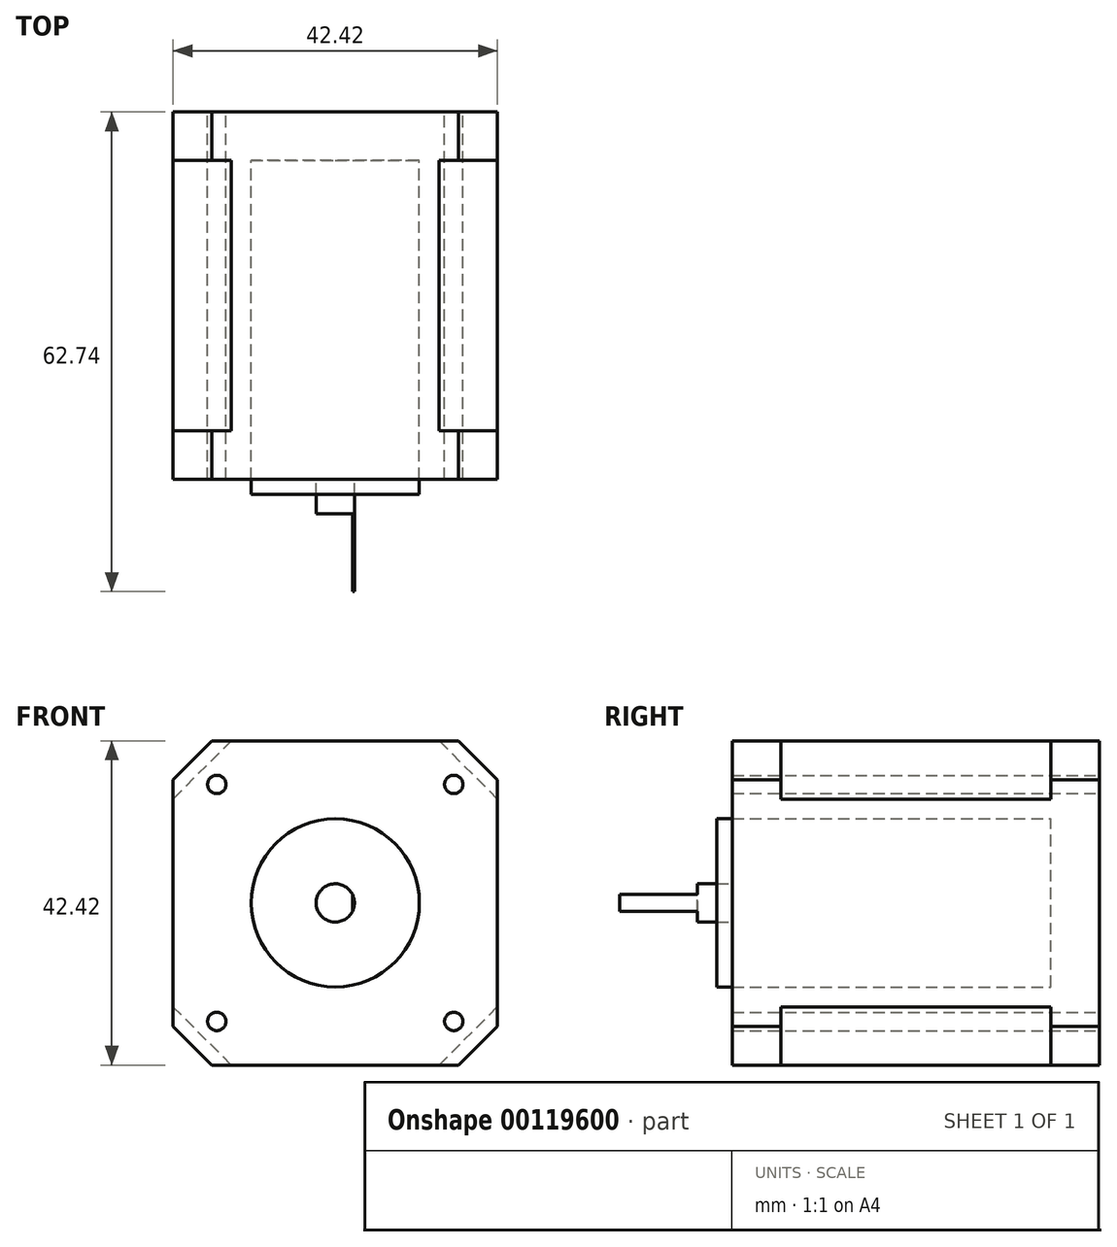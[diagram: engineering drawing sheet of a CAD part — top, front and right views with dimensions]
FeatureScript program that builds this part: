
annotation { "Feature Type Name" : "Feature", "Feature Type Description" : "" }
export const myFeature = defineFeature(function(context is Context, id is Id, definition is map)
    precondition{}
    {
        {
            var Q0;
            Q0=qCreatedBy(makeId("Front.planeOp"),FACE);
            var sketch = newSketch(context, id + "F0", { "sketchPlane" : qUnion([Q0])});
            skPoint(sketch, "E0.middle", {"position": v(0, 0) * mm});
            skLineSegment(sketch, "E1.bottom", {"start": v(-16.13, -21.2) * mm, "end": v(16.13, -21.2) * mm});
            skLineSegment(sketch, "E1.top", {"start": v(-16.13, 21.21) * mm, "end": v(16.13, 21.21) * mm});
            skLineSegment(sketch, "E1.left", {"start": v(-21.21, -16.13) * mm, "end": v(-21.21, 16.13) * mm});
            skLineSegment(sketch, "E1.right", {"start": v(21.2, -16.13) * mm, "end": v(21.2, 16.13) * mm});
            skCircle(sketch, "E2", {"center": v(0, 0) * mm, "radius": 11 * mm});
            skCircle(sketch, "E3", {"center": v(0, 0) * mm, "radius": 2.5 * mm});
            skCircle(sketch, "E4", {"center": v(15.5, 15.5) * mm, "radius": 1.2 * mm});
            skCircle(sketch, "E5.MirrorC", {"center": v(-15.5, 15.5) * mm, "radius": 1.2 * mm});
            skCircle(sketch, "E6.MirrorC", {"center": v(15.5, -15.5) * mm, "radius": 1.2 * mm});
            skCircle(sketch, "E7.MirrorC", {"center": v(-15.5, -15.5) * mm, "radius": 1.2 * mm});
            skLineSegment(sketch, "E8", {"start": v(-16.13, 21.21) * mm, "end": v(-21.21, 16.13) * mm});
            skLineSegment(sketch, "E9", {"start": v(-21.21, -16.13) * mm, "end": v(-16.13, -21.2) * mm});
            skLineSegment(sketch, "E10", {"start": v(16.13, -21.2) * mm, "end": v(21.2, -16.13) * mm});
            skLineSegment(sketch, "E11", {"start": v(21.2, 16.13) * mm, "end": v(16.13, 21.21) * mm});
            skLineSegment(sketch, "E12", {"start": v(-13.6, 21.21) * mm, "end": v(-21.21, 13.59) * mm});
            skLineSegment(sketch, "E13", {"start": v(-21.21, -13.59) * mm, "end": v(-13.59, -21.2) * mm});
            skLineSegment(sketch, "E14", {"start": v(13.59, -21.2) * mm, "end": v(21.2, -13.59) * mm});
            skLineSegment(sketch, "E15", {"start": v(21.2, 13.6) * mm, "end": v(13.59, 21.21) * mm});
            skLineSegment(sketch, "E16.bottom", {"start": v(2.75, -2.5) * mm, "end": v(2.25, -2.5) * mm});
            skLineSegment(sketch, "E16.top", {"start": v(2.75, 2.5) * mm, "end": v(2.25, 2.5) * mm});
            skLineSegment(sketch, "E16.left", {"start": v(2.75, -2.5) * mm, "end": v(2.75, 2.5) * mm});
            skLineSegment(sketch, "E16.right", {"start": v(2.25, -2.5) * mm, "end": v(2.25, 2.5) * mm});
            skPoint(sketch, "E16.middle", {"position": v(2.5, 0) * mm});
            skSolve(sketch);
        }
        {
            var Q0;
            {var subQ0=sQuery(id+"F0.wireOp",EDGE,"E16.right");var subQ1=sQuery(id+"F0.wireOp",EDGE,"E3");var subQ2=makeQuery(id+"F0.imprint","INTERSECT",VERTEX,{"disambiguationData":[OD(0.0)],"derivedFrom":[subQ1,subQ0]});Q0=makeQuery(id+"F0.imprint","IMPRINT",FACE,{"disambiguationData":[TD([[makeQuery(id+"F0.imprint","IMPRINT",EDGE,{"disambiguationData":[TD([[subQ2,1.0]])],"derivedFrom":subQ1}),1.0]])]});}
            extrude(context, id + "F1", {"entities" : qUnion([Q0]), "depth" : 62.74 * mm, "hasSecondDirection" : true, "secondDirectionOppositeDirection" : false, "secondDirectionDepth" : 52.58 * mm});
        }
        {
            var Q0;
            {var subQ0=sQuery(id+"F0.wireOp",EDGE,"E16.right");var subQ1=sQuery(id+"F0.wireOp",EDGE,"E3");var subQ2=makeQuery(id+"F0.imprint","INTERSECT",VERTEX,{"disambiguationData":[OD(0.0)],"derivedFrom":[subQ1,subQ0]});Q0=makeQuery(id+"F0.imprint","IMPRINT",FACE,{"disambiguationData":[TD([[makeQuery(id+"F0.imprint","IMPRINT",EDGE,{"disambiguationData":[TD([[subQ2,-1.0]])],"derivedFrom":subQ1}),1.0]])]});}
            var Q1;
            {var subQ0=sQuery(id+"F0.wireOp",EDGE,"E16.right");var subQ1=sQuery(id+"F0.wireOp",EDGE,"E3");var subQ2=makeQuery(id+"F0.imprint","INTERSECT",VERTEX,{"disambiguationData":[OD(0.0)],"derivedFrom":[subQ1,subQ0]});Q1=makeQuery(id+"F0.imprint","IMPRINT",FACE,{"disambiguationData":[TD([[makeQuery(id+"F0.imprint","IMPRINT",EDGE,{"disambiguationData":[TD([[subQ2,1.0]])],"derivedFrom":subQ1}),1.0]])]});}
            extrude(context, id + "F2", {"entities" : qUnion([Q0, Q1]), "operationType" : NewBodyOperationType.ADD, "depth" : 52.58 * mm, "hasSecondDirection" : true, "secondDirectionOppositeDirection" : false, "secondDirectionDepth" : 50.04 * mm});
        }
        {
            var Q0;
            Q0=makeQuery(id+"F0.imprint","IMPRINT",FACE,{"disambiguationData":[TD([[makeQuery(id+"F0.imprint","IMPRINT",EDGE,{"derivedFrom":sQuery(id+"F0.wireOp",EDGE,"E2")}),1.0]])]});
            var Q1;
            {var subQ4=sQuery(id+"F0.wireOp",EDGE,"E16.bottom");Q1=makeQuery(id+"F0.imprint","IMPRINT",FACE,{"disambiguationData":[TD([[makeQuery(id+"F0.imprint","IMPRINT",EDGE,{"derivedFrom":subQ4}),-1.0]])]});}
            extrude(context, id + "F3", {"entities" : qUnion([Q0, Q1]), "depth" : 50.04 * mm, "hasSecondDirection" : true, "secondDirectionOppositeDirection" : false, "secondDirectionDepth" : 48 * mm});
        }
        {
            var Q0;
            Q0=makeQuery(id+"F0.imprint","IMPRINT",FACE,{"disambiguationData":[TD([[makeQuery(id+"F0.imprint","IMPRINT",EDGE,{"derivedFrom":sQuery(id+"F0.wireOp",EDGE,"E2")}),-1.0]])]});
            var Q1;
            {var subQ0=sQuery(id+"F0.wireOp",EDGE,"E11");Q1=makeQuery(id+"F0.imprint","IMPRINT",FACE,{"disambiguationData":[TD([[makeQuery(id+"F0.imprint","IMPRINT",EDGE,{"derivedFrom":subQ0}),1.0]])]});}
            var Q2;
            {var subQ0=sQuery(id+"F0.wireOp",EDGE,"E10");Q2=makeQuery(id+"F0.imprint","IMPRINT",FACE,{"disambiguationData":[TD([[makeQuery(id+"F0.imprint","IMPRINT",EDGE,{"derivedFrom":subQ0}),1.0]])]});}
            var Q3;
            {var subQ0=sQuery(id+"F0.wireOp",EDGE,"E9");Q3=makeQuery(id+"F0.imprint","IMPRINT",FACE,{"disambiguationData":[TD([[makeQuery(id+"F0.imprint","IMPRINT",EDGE,{"derivedFrom":subQ0}),1.0]])]});}
            var Q4;
            {var subQ0=sQuery(id+"F0.wireOp",EDGE,"E8");Q4=makeQuery(id+"F0.imprint","IMPRINT",FACE,{"disambiguationData":[TD([[makeQuery(id+"F0.imprint","IMPRINT",EDGE,{"derivedFrom":subQ0}),1.0]])]});}
            extrude(context, id + "F4", {"entities" : qUnion([Q0, Q1, Q2, Q3, Q4]), "depth" : 48 * mm, "hasSecondDirection" : true, "secondDirectionOppositeDirection" : false, "secondDirectionDepth" : 41.66 * mm});
        }
        {
            var Q0;
            Q0=makeQuery(id+"F0.imprint","IMPRINT",FACE,{"disambiguationData":[TD([[makeQuery(id+"F0.imprint","IMPRINT",EDGE,{"derivedFrom":sQuery(id+"F0.wireOp",EDGE,"E2")}),-1.0]])]});
            extrude(context, id + "F5", {"entities" : qUnion([Q0]), "operationType" : NewBodyOperationType.ADD, "depth" : 41.66 * mm, "hasSecondDirection" : true, "secondDirectionOppositeDirection" : false, "secondDirectionDepth" : 6.35 * mm});
        }
        {
            var Q0;
            {var subQ0=sQuery(id+"F0.wireOp",EDGE,"E9");Q0=makeQuery(id+"F0.imprint","IMPRINT",FACE,{"disambiguationData":[TD([[makeQuery(id+"F0.imprint","IMPRINT",EDGE,{"derivedFrom":subQ0}),1.0]])]});}
            var Q1;
            {var subQ0=sQuery(id+"F0.wireOp",EDGE,"E8");Q1=makeQuery(id+"F0.imprint","IMPRINT",FACE,{"disambiguationData":[TD([[makeQuery(id+"F0.imprint","IMPRINT",EDGE,{"derivedFrom":subQ0}),1.0]])]});}
            var Q2;
            {var subQ0=sQuery(id+"F0.wireOp",EDGE,"E11");Q2=makeQuery(id+"F0.imprint","IMPRINT",FACE,{"disambiguationData":[TD([[makeQuery(id+"F0.imprint","IMPRINT",EDGE,{"derivedFrom":subQ0}),1.0]])]});}
            var Q3;
            {var subQ0=sQuery(id+"F0.wireOp",EDGE,"E10");Q3=makeQuery(id+"F0.imprint","IMPRINT",FACE,{"disambiguationData":[TD([[makeQuery(id+"F0.imprint","IMPRINT",EDGE,{"derivedFrom":subQ0}),1.0]])]});}
            var Q4;
            Q4=makeQuery(id+"F0.imprint","IMPRINT",FACE,{"disambiguationData":[TD([[makeQuery(id+"F0.imprint","IMPRINT",EDGE,{"derivedFrom":sQuery(id+"F0.wireOp",EDGE,"E6.MirrorC")}),-1.0]])]});
            var Q5;
            Q5=makeQuery(id+"F0.imprint","IMPRINT",FACE,{"disambiguationData":[TD([[makeQuery(id+"F0.imprint","IMPRINT",EDGE,{"derivedFrom":sQuery(id+"F0.wireOp",EDGE,"E4")}),1.0]])]});
            var Q6;
            Q6=makeQuery(id+"F0.imprint","IMPRINT",FACE,{"disambiguationData":[TD([[makeQuery(id+"F0.imprint","IMPRINT",EDGE,{"derivedFrom":sQuery(id+"F0.wireOp",EDGE,"E5.MirrorC")}),-1.0]])]});
            var Q7;
            Q7=makeQuery(id+"F0.imprint","IMPRINT",FACE,{"disambiguationData":[TD([[makeQuery(id+"F0.imprint","IMPRINT",EDGE,{"derivedFrom":sQuery(id+"F0.wireOp",EDGE,"E7.MirrorC")}),1.0]])]});
            var Q8;
            Q8=makeQuery(id+"F0.imprint","IMPRINT",FACE,{"disambiguationData":[TD([[makeQuery(id+"F0.imprint","IMPRINT",EDGE,{"derivedFrom":sQuery(id+"F0.wireOp",EDGE,"E2")}),-1.0]])]});
            var Q9;
            {var subQ4=sQuery(id+"F0.wireOp",EDGE,"E16.bottom");Q9=makeQuery(id+"F0.imprint","IMPRINT",FACE,{"disambiguationData":[TD([[makeQuery(id+"F0.imprint","IMPRINT",EDGE,{"derivedFrom":subQ4}),-1.0]])]});}
            var Q10;
            {var subQ0=sQuery(id+"F0.wireOp",EDGE,"E16.right");var subQ1=sQuery(id+"F0.wireOp",EDGE,"E3");var subQ2=makeQuery(id+"F0.imprint","INTERSECT",VERTEX,{"disambiguationData":[OD(0.0)],"derivedFrom":[subQ1,subQ0]});Q10=makeQuery(id+"F0.imprint","IMPRINT",FACE,{"disambiguationData":[TD([[makeQuery(id+"F0.imprint","IMPRINT",EDGE,{"disambiguationData":[TD([[subQ2,-1.0]])],"derivedFrom":subQ1}),1.0]])]});}
            var Q11;
            {var subQ0=sQuery(id+"F0.wireOp",EDGE,"E16.right");var subQ1=sQuery(id+"F0.wireOp",EDGE,"E3");var subQ2=makeQuery(id+"F0.imprint","INTERSECT",VERTEX,{"disambiguationData":[OD(0.0)],"derivedFrom":[subQ1,subQ0]});Q11=makeQuery(id+"F0.imprint","IMPRINT",FACE,{"disambiguationData":[TD([[makeQuery(id+"F0.imprint","IMPRINT",EDGE,{"disambiguationData":[TD([[subQ2,1.0]])],"derivedFrom":subQ1}),1.0]])]});}
            var Q12;
            Q12=makeQuery(id+"F0.imprint","IMPRINT",FACE,{"disambiguationData":[TD([[makeQuery(id+"F0.imprint","IMPRINT",EDGE,{"derivedFrom":sQuery(id+"F0.wireOp",EDGE,"E2")}),1.0]])]});
            extrude(context, id + "F6", {"entities" : qUnion([Q0, Q1, Q2, Q3, Q4, Q5, Q6, Q7, Q8, Q9, Q10, Q11, Q12]), "operationType" : NewBodyOperationType.ADD, "depth" : 6.35 * mm});
        }
    });
